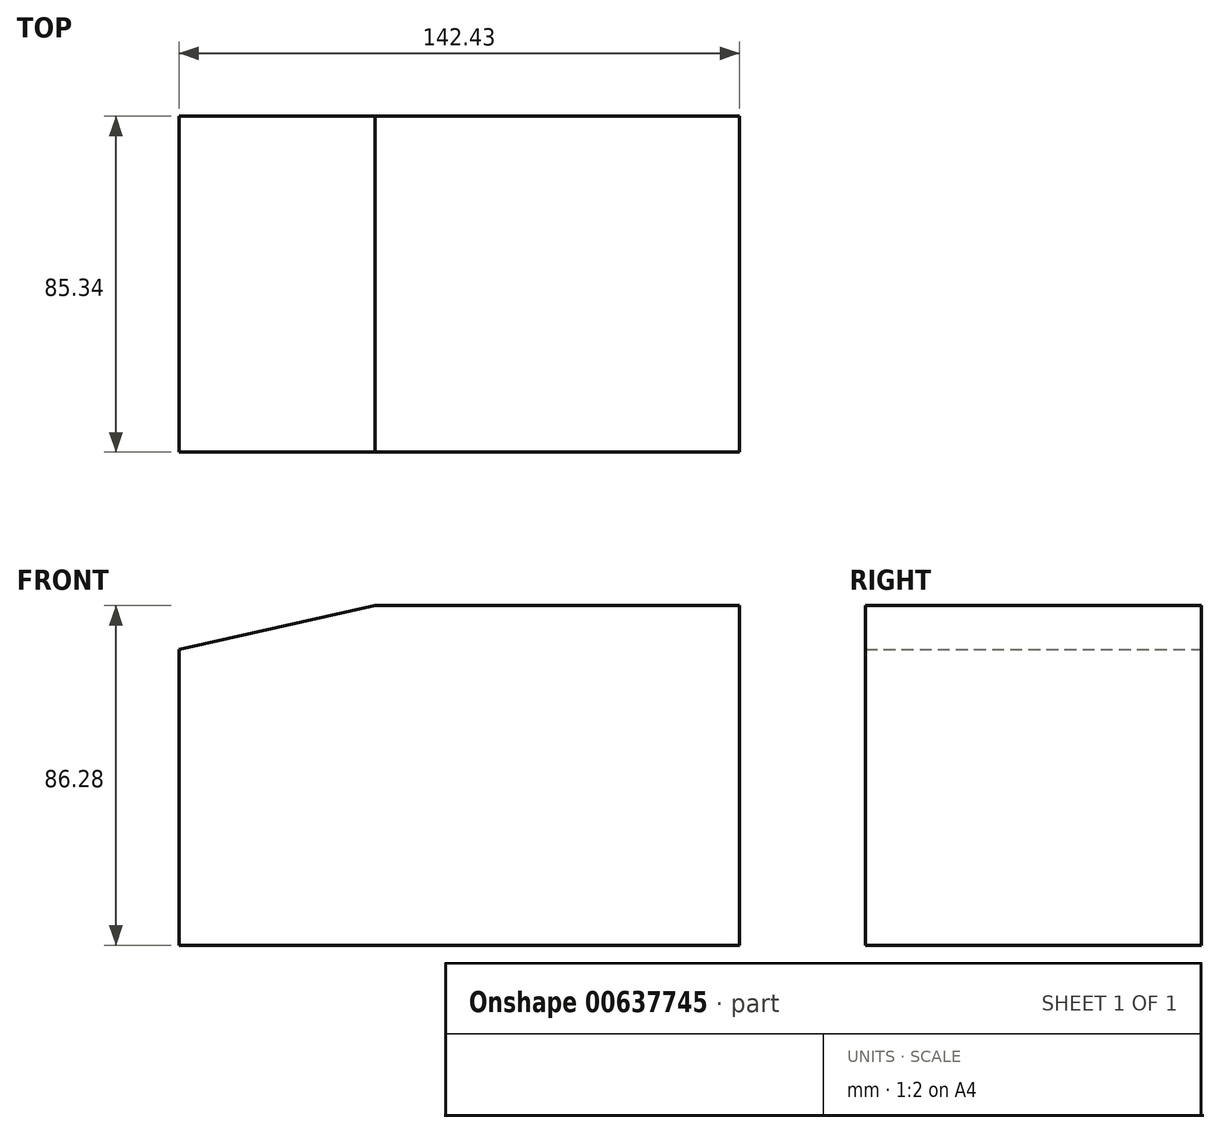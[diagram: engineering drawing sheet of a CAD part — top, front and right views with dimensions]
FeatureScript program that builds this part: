
annotation { "Feature Type Name" : "Feature", "Feature Type Description" : "" }
export const myFeature = defineFeature(function(context is Context, id is Id, definition is map)
    precondition{}
    {
        {
            var Q0;
            Q0=qCreatedBy(makeId("Front.planeOp"),FACE);
            var sketch = newSketch(context, id + "F0", { "sketchPlane" : qUnion([Q0])});
            skLineSegment(sketch, "E0.bottom", {"start": v(-66.31, 42.68) * mm, "end": v(76.12, 42.68) * mm});
            skLineSegment(sketch, "E0.top", {"start": v(-66.31, -43.6) * mm, "end": v(76.12, -43.6) * mm});
            skLineSegment(sketch, "E0.left", {"start": v(-66.31, 42.68) * mm, "end": v(-66.31, -43.6) * mm});
            skLineSegment(sketch, "E0.right", {"start": v(76.12, 42.68) * mm, "end": v(76.12, -43.6) * mm});
            skSolve(sketch);
        }
        {
            var Q0;
            Q0 = qSketchRegion(id + "FwSovdds70wunu3_0", true);
            var Q1;
            Q1=makeQuery(id+"F0.imprint","IMPRINT",FACE,{"disambiguationData":[TD([[makeQuery(id+"F0.imprint","IMPRINT",EDGE,{"derivedFrom":sQuery(id+"F0.wireOp",EDGE,"E0.bottom")}),-1.0]])]});
            extrude(context, id + "F1", {"entities" : qUnion([Q0, Q1]), "depth" : 85.34 * mm, "offsetDistance" : 25.4 * mm});
        }
        {
            var Q0;
            Q0=makeQuery(id+"F1.opExtrude","CAP_FACE",FACE,{"disambiguationData":[OSD([sQuery(id+"F0.wireOp",EDGE,"E0.bottom"),sQuery(id+"F0.wireOp",EDGE,"E0.top"),sQuery(id+"F0.wireOp",EDGE,"E0.left"),sQuery(id+"F0.wireOp",EDGE,"E0.right")])],"isStart":true});
            var sketch = newSketch(context, id + "F2", { "sketchPlane" : qUnion([Q0])});
            skLineSegment(sketch, "E1", {"start": v(66.31, 31.5) * mm, "end": v(16.52, 42.68) * mm});
            skSolve(sketch);
        }
        {
            var Q0;
            {var subQ0=sQuery(id+"F2.wireOp",EDGE,"E1");Q0=makeQuery(id+"F2.imprint","IMPRINT",FACE,{"disambiguationData":[TD([[makeQuery(id+"F2.imprint","IMPRINT",EDGE,{"derivedFrom":subQ0}),-1.0]])]});}
            extrude(context, id + "F3", {"entities" : qUnion([Q0]), "operationType" : NewBodyOperationType.REMOVE, "oppositeDirection" : true, "depth" : 101.6 * mm, "offsetDistance" : 25.4 * mm});
        }
    });
